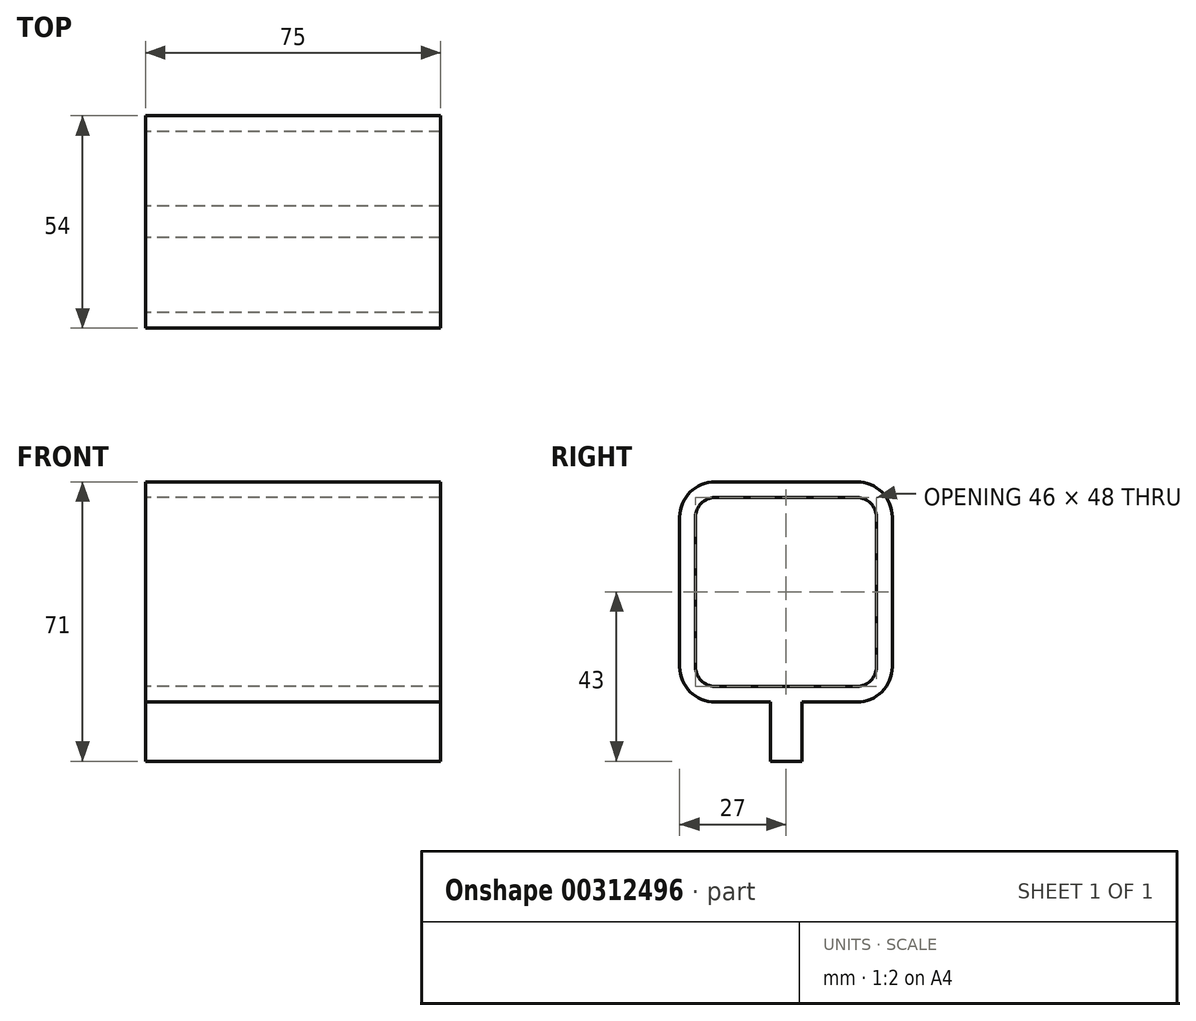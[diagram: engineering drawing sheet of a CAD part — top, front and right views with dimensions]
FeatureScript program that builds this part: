
annotation { "Feature Type Name" : "Feature", "Feature Type Description" : "" }
export const myFeature = defineFeature(function(context is Context, id is Id, definition is map)
    precondition{}
    {
        {
            var Q0;
            Q0=qCreatedBy(makeId("Right.planeOp"),FACE);
            var sketch = newSketch(context, id + "F0", { "sketchPlane" : qUnion([Q0])});
            skLineSegment(sketch, "E0.bottom", {"start": v(-41, 48) * mm, "end": v(-5, 48) * mm});
            skLineSegment(sketch, "E0.left", {"start": v(-46, 43) * mm, "end": v(-46, 5) * mm});
            skLineSegment(sketch, "E0.right", {"start": v(0, 43) * mm, "end": v(0, 5) * mm});
            skPoint(sketch, "E1.visualSharp", {"position": v(-46, 48) * mm});
            skArc(sketch, "E1.filletArc", {"start": v(-41, 48) * mm, "mid": v(-44.54, 46.54) * mm, "end": v(-46, 43) * mm});
            skPoint(sketch, "E2.visualSharp", {"position": v(-46, 0) * mm});
            skArc(sketch, "E2.filletArc", {"start": v(-46, 5) * mm, "mid": v(-44.54, 1.46) * mm, "end": v(-41, 0) * mm});
            skPoint(sketch, "E3.visualSharp", {"position": v(0, 0) * mm});
            skArc(sketch, "E3.filletArc", {"start": v(-5, 0) * mm, "mid": v(-1.46, 1.46) * mm, "end": v(0, 5) * mm});
            skPoint(sketch, "E4.visualSharp", {"position": v(0, 48) * mm});
            skArc(sketch, "E4.filletArc", {"start": v(0, 43) * mm, "mid": v(-1.46, 46.54) * mm, "end": v(-5, 48) * mm});
            skArc(sketch, "E5.0", {"start": v(-41, 52) * mm, "mid": v(-47.36, 49.36) * mm, "end": v(-50, 43) * mm});
            skLineSegment(sketch, "E5.1", {"start": v(-50, 43) * mm, "end": v(-50, 5) * mm});
            skLineSegment(sketch, "E5.2", {"start": v(-41, 52) * mm, "end": v(-5, 52) * mm});
            skArc(sketch, "E5.3", {"start": v(-50, 5) * mm, "mid": v(-47.36, -1.36) * mm, "end": v(-41, -4) * mm});
            skArc(sketch, "E5.4", {"start": v(4, 43) * mm, "mid": v(1.36, 49.36) * mm, "end": v(-5, 52) * mm});
            skLineSegment(sketch, "E5.5", {"start": v(4, 43) * mm, "end": v(4, 5) * mm});
            skArc(sketch, "E5.6", {"start": v(-5, -4) * mm, "mid": v(1.36, -1.36) * mm, "end": v(4, 5) * mm});
            skLineSegment(sketch, "E6", {"start": v(-41, -4) * mm, "end": v(-27, -4) * mm});
            skLineSegment(sketch, "E7", {"start": v(-27, -4) * mm, "end": v(-27, -19) * mm});
            skLineSegment(sketch, "E8", {"start": v(-19, -19) * mm, "end": v(-19, -4) * mm});
            skLineSegment(sketch, "E9", {"start": v(-19, -4) * mm, "end": v(-5, -4) * mm});
            skLineSegment(sketch, "E10", {"start": v(-41, 0) * mm, "end": v(-23, 0) * mm});
            skLineSegment(sketch, "E11", {"start": v(-23, 0) * mm, "end": v(-23, -19) * mm});
            skLineSegment(sketch, "E12", {"start": v(-23, -19) * mm, "end": v(-27, -19) * mm});
            skLineSegment(sketch, "E13", {"start": v(-19, -19) * mm, "end": v(-23, -19) * mm});
            skLineSegment(sketch, "E14", {"start": v(-23, -19) * mm, "end": v(-23, 0) * mm});
            skLineSegment(sketch, "E15", {"start": v(-23, 0) * mm, "end": v(-5, 0) * mm});
            skSolve(sketch);
        }
        {
            var Q0;
            Q0=makeQuery(id+"F0.imprint","IMPRINT",FACE,{"disambiguationData":[TD([[makeQuery(id+"F0.imprint","IMPRINT",EDGE,{"derivedFrom":sQuery(id+"F0.wireOp",EDGE,"E0.bottom")}),1.0]])]});
            extrude(context, id + "F1", {"entities" : qUnion([Q0]), "depth" : 75 * mm});
        }
    });
